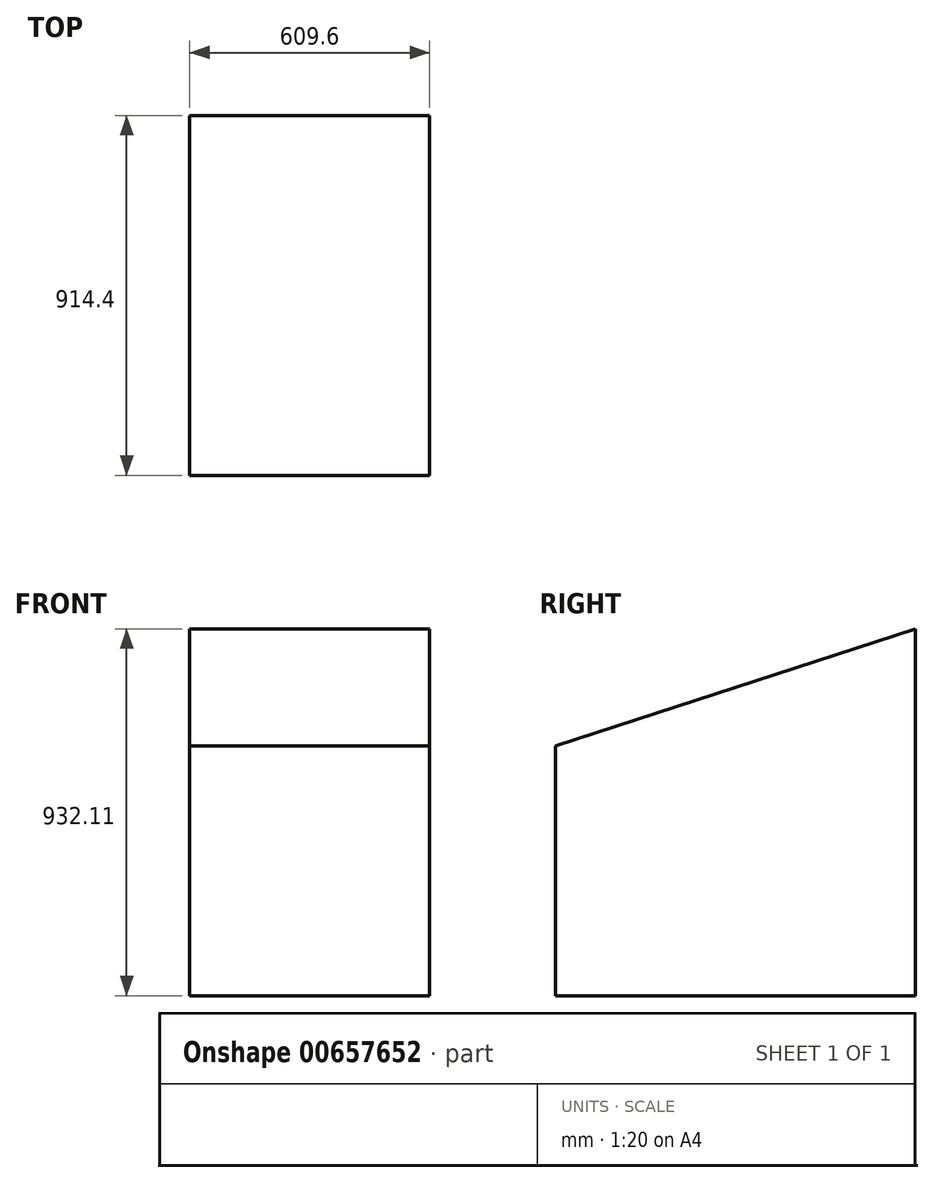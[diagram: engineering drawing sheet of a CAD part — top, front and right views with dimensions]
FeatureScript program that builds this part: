
annotation { "Feature Type Name" : "Feature", "Feature Type Description" : "" }
export const myFeature = defineFeature(function(context is Context, id is Id, definition is map)
    precondition{}
    {
        {
            var Q0;
            Q0=qCreatedBy(makeId("Top.planeOp"),FACE);
            var sketch = newSketch(context, id + "F0", { "sketchPlane" : qUnion([Q0])});
            skLineSegment(sketch, "E0.bottom", {"start": v(0, 0) * mm, "end": v(609.6, 0) * mm});
            skLineSegment(sketch, "E0.top", {"start": v(0, -914.4) * mm, "end": v(609.6, -914.4) * mm});
            skLineSegment(sketch, "E0.left", {"start": v(0, 0) * mm, "end": v(0, -914.4) * mm});
            skLineSegment(sketch, "E0.right", {"start": v(609.6, 0) * mm, "end": v(609.6, -914.4) * mm});
            skSolve(sketch);
        }
        {
            var Q0;
            Q0=makeQuery(id+"F0.imprint","IMPRINT",FACE,{"disambiguationData":[TD([[makeQuery(id+"F0.imprint","IMPRINT",EDGE,{"derivedFrom":sQuery(id+"F0.wireOp",EDGE,"E0.bottom")}),-1.0]])]});
            extrude(context, id + "F1", {"entities" : qUnion([Q0]), "depth" : 635 * mm, "offsetDistance" : 25.4 * mm});
        }
        {
            var Q0;
            Q0=makeQuery(id+"F1.opExtrude","SWEPT_FACE",FACE,{"disambiguationData":[OSD([sQuery(id+"F0.wireOp",EDGE,"E0.right")])]});
            var sketch = newSketch(context, id + "F2", { "sketchPlane" : qUnion([Q0])});
            skLineSegment(sketch, "E1", {"start": v(-914.4, 635) * mm, "end": v(0, 932.1) * mm});
            skLineSegment(sketch, "E2", {"start": v(0, 932.1) * mm, "end": v(0, 635) * mm});
            skSolve(sketch);
        }
        {
            var Q0;
            Q0=makeQuery(id+"F2.imprint","IMPRINT",FACE,{"disambiguationData":[TD([[makeQuery(id+"F2.imprint","IMPRINT",EDGE,{"derivedFrom":sQuery(id+"F2.wireOp",EDGE,"E1")}),-1.0]])]});
            extrude(context, id + "F3", {"entities" : qUnion([Q0]), "operationType" : NewBodyOperationType.ADD, "oppositeDirection" : true, "depth" : 609.6 * mm, "offsetDistance" : 25.4 * mm});
        }
    });
